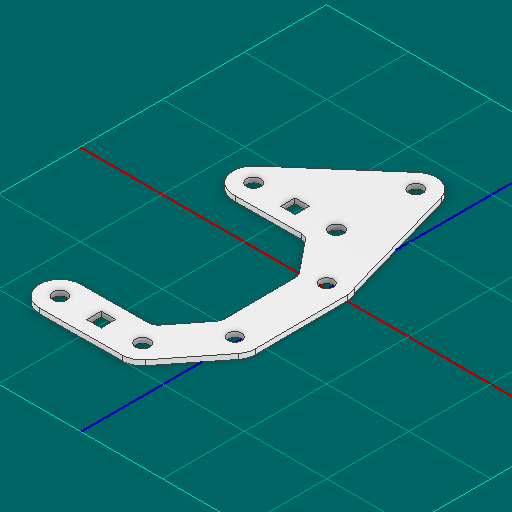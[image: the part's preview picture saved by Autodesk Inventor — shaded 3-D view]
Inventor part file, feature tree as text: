
AUTODESK INVENTOR PART (.ipt)
format: ipt  version: 2025 (Build 290162000, 162)  size: 187,904 bytes
history: native  units: in
note: dims shown in document units (in); Inventor stores cm internally (conversion verified against a paired STEP export)
features: other x6, sketch x1
ambient origin geometry x8: Origin, YZ Plane, XZ Plane, XY Plane, X Axis, Y Axis, Z Axis, Center Point
bodies: Solid1 (feature_tree)
feature tree (7):
  other  "funnel_gusset.ipt"
  other  "Blocks"
  other  "main_gusset"
  other  "Solid1::funnel_gusset.ipt"
  other  "TaggingFeature1"
  sketch  "Sketch1"  dims[d0=0.3937in d1=0.5in d2=0.5in d3=0.125in d6=0.176in d7=0.176in d8=0.176in d9=0.176in d10=0.5in d11=0.5in d12=0.25in d13=0.25in d14=0.625in d15=0.625in d16=0.5in]
  other  "main_gusset:1"
